# Revit family: F1000-C & F1100-C
name_source: partatom
category: Plumbing Fixtures
revit_build: Autodesk Revit 2017 (Build: 20190508_0315(x64)
units: mm (PartAtom-declared; Revit-internal decimal feet)

## family parameters
Cut with Voids When Loaded = No
Host = Face
Part Type = Normal
Room Calculation Point = No
Round Connector Dimension = Use Radius
Shared = No

## types (25) — shared parameters
Body Height = 0' - 4 1/2"
Default Elevation = 0' - 0"
Domestic Cold Water Diameter = 0' - 0 1/2"
Domestic Cold Water Radius = 0' - 0 1/2"
Floor Drain Material = Paint - Sherwin Williams Paint - #952C2A - Bellwood Red
Manufacturer = MIFAB
Strainer Diameter = 0' - 7"
URL = WWW.MIFAB.COM
zero-valued in all types: CWFU, WFU

## per-type parameters (varying)
| type | Description | Model | Pipe Diameter | Pipe Radius | Top Diameter |
| 8" Dia  Strainer - 3" Drain | FLOOR DRAIN WITH ROUND ADJUSTABLE STAINLESS STEEL STRAINER | F1000-C/F1100-C | 0' - 3" | 0' - 1 1/2" | 0' - 8" |
| 8" Dia  Strainer - 5" Drain | FLOOR DRAIN WITH ROUND ADJUSTABLE STAINLESS STEEL STRAINER | F1000-C/F1100-C | 0' - 5" | 0' - 2 1/2" | 0' - 8" |
| 8" Dia  Strainer - 6" Drain | FLOOR DRAIN WITH ROUND ADJUSTABLE STAINLESS STEEL STRAINER | F1000-C/F1100-C | 0' - 6" | 0' - 3" | 0' - 8" |
| 5" Dia  Strainer - 6" Drain | FLOOR DRAIN WITH ROUND ADJUSTABLE STAINLESS STEEL STRAINER | F1100-C-S | 0' - 6" | 0' - 3" | 0' - 5" |
| 6" Dia  Strainer - 6" Drain | FLOOR DRAIN WITH ROUND ADJUSTABLE STAINLESS STEEL STRAINER | F1000-C/F1100-C | 0' - 6" | 0' - 3" | 0' - 6" |
| 5" Dia  Strainer - 3" Drain | FLOOR DRAIN WITH ROUND ADJUSTABLE STAINLESS STEEL STRAINER | F1100-C-S | 0' - 3" | 0' - 1 1/2" | 0' - 5" |
| 5" Dia  Strainer - 4" Drain | SQUARE FLOOR DRAIN | F1000-C/F1100-C | 0' - 4" | 0' - 2" | 0' - 5" |
| 5" Dia  Strainer - 5" Drain | FLOOR DRAIN WITH ROUND ADJUSTABLE STAINLESS STEEL STRAINER | F1000-C/F1100-C | 0' - 5" | 0' - 2 1/2" | 0' - 5" |
| 8" Dia  Strainer - 2" Drain | FLOOR DRAIN WITH ROUND ADJUSTABLE STAINLESS STEEL STRAINER | F1000-C/F1100-C | 0' - 2" | 0' - 1" | 0' - 8" |
| 6" Dia  Strainer - 3" Drain | FLOOR DRAIN WITH ROUND ADJUSTABLE STAINLESS STEEL STRAINER | F1000-C/F1100-C | 0' - 3" | 0' - 1 1/2" | 0' - 6" |
| 6" Dia  Strainer - 4" Drain | FLOOR DRAIN WITH ROUND ADJUSTABLE STAINLESS STEEL STRAINER | F1000-C/F1100-C | 0' - 4" | 0' - 2" | 0' - 6" |
| 6" Dia  Strainer - 5" Drain | FLOOR DRAIN WITH ROUND ADJUSTABLE STAINLESS STEEL STRAINER | F1000-C/F1100-C | 0' - 5" | 0' - 2 1/2" | 0' - 6" |
| 6" Dia  Strainer - 2" Drain | FLOOR DRAIN WITH ROUND ADJUSTABLE STAINLESS STEEL STRAINER | F1000-C/F1100-C | 0' - 2" | 0' - 1" | 0' - 6" |
| 10" Dia  Strainer - 2" Drain | FLOOR DRAIN WITH ROUND ADJUSTABLE STAINLESS STEEL STRAINER | F1000-C/F1100-C | 0' - 2" | 0' - 1" | 0' - 10" |
| 10" Dia  Strainer - 3" Drain | FLOOR DRAIN WITH ROUND ADJUSTABLE STAINLESS STEEL STRAINER | F1000-C/F1100-C | 0' - 3" | 0' - 1 1/2" | 0' - 10" |
| 8" Dia  Strainer - 4" Drain | FLOOR DRAIN WITH ROUND ADJUSTABLE STAINLESS STEEL STRAINER | F1000-C/F1100-C | 0' - 4" | 0' - 2" | 0' - 8" |
| 10" Dia  Strainer - 4" Drain | FLOOR DRAIN WITH ROUND ADJUSTABLE STAINLESS STEEL STRAINER | F1000-C/F1100-C | 0' - 4" | 0' - 2" | 0' - 10" |
| 10" Dia  Strainer - 5" Drain | FLOOR DRAIN WITH ROUND ADJUSTABLE STAINLESS STEEL STRAINER | F1000-C/F1100-C | 0' - 5" | 0' - 2 1/2" | 0' - 10" |
| 10" Dia  Strainer - 6" Drain | FLOOR DRAIN WITH ROUND ADJUSTABLE STAINLESS STEEL STRAINER | F1100-C-S | 0' - 6" | 0' - 3" | 0' - 10" |
| 5" Dia  Strainer - 2" Drain | FLOOR DRAIN WITH ROUND ADJUSTABLE STAINLESS STEEL STRAINER | F1000-C/F1100-C | 0' - 2" | 0' - 1" | 0' - 5" |
| 7" Dia  Strainer - 2" Drain | FLOOR DRAIN WITH ROUND ADJUSTABLE STAINLESS STEEL STRAINER | F1000-C/F1100-C | 0' - 2" | 0' - 1" | 0' - 7" |
| 7" Dia  Strainer - 3" Drain | FLOOR DRAIN WITH ROUND ADJUSTABLE STAINLESS STEEL STRAINER | F1000-C/F1100-C | 0' - 3" | 0' - 1 1/2" | 0' - 7" |
| 7" Dia  Strainer - 4" Drain | FLOOR DRAIN WITH ROUND ADJUSTABLE STAINLESS STEEL STRAINER | F1000-C/F1100-C | 0' - 4" | 0' - 2" | 0' - 7" |
| 7" Dia  Strainer - 5" Drain | FLOOR DRAIN WITH ROUND ADJUSTABLE STAINLESS STEEL STRAINER | F1000-C/F1100-C | 0' - 5" | 0' - 2 1/2" | 0' - 7" |
| 7" Dia  Strainer - 6" Drain | FLOOR DRAIN WITH ROUND ADJUSTABLE STAINLESS STEEL STRAINER | F1000-C/F1100-C | 0' - 6" | 0' - 3" | 0' - 7" |

## geometry (parser evidence)
native form markers: Sweep x4
no freeform markers — native parametric forms only
